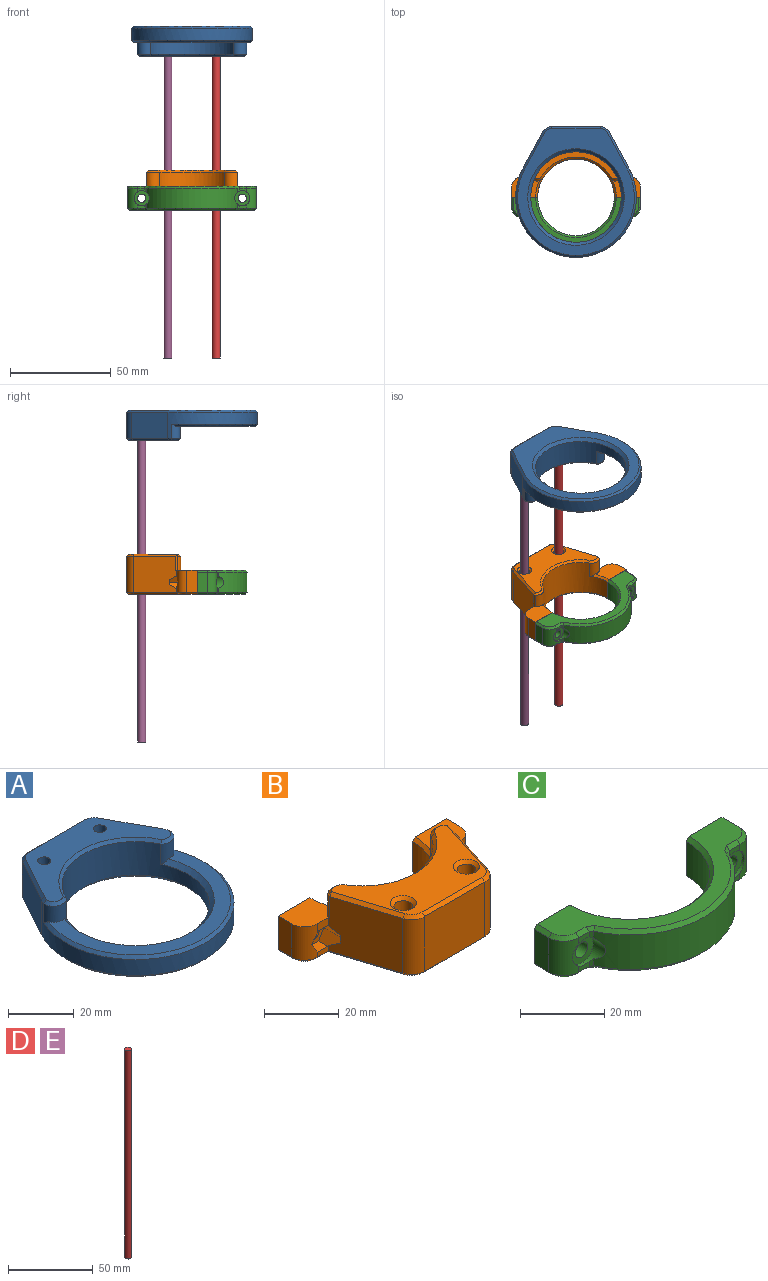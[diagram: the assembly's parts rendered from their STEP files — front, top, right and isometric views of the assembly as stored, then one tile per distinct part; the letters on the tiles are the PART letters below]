
ASSEMBLY  parts=5 mates=4
PART A: 39 faces, bbox 60x65x15 mm
  f0: plane 58x39.83mm, normal (0,0,1), area 508.6mm2, adj f11,f12,f17,f24
  f1: plane 17.96x13mm, normal (-0.88,0.48,0), area 266.4mm2, adj f2,f7,f20,f34
  f2: cylinder r=30mm len=60mm, axis (0,0,-1), area 771.3mm2, adj f1,f3,f18,f21,f24,f27,f32,f33
  f3: plane 17.96x13mm, normal (0.88,0.48,0), area 266.4mm2, adj f2,f4,f31,f35
  f4: cylinder r=5mm len=13mm, axis (0,0,-1), area 69.4mm2, adj f3,f5,f29,f37
  f5: plane 24.08x13mm, normal (0,1,0), area 313.1mm2, adj f4,f7,f26,f38
  f6: cylinder r=2mm len=13mm, axis (0,0,-1), area 163.4mm2, adj f13,f15
  f7: cylinder r=5mm len=13mm, axis (0,0,-1), area 69.4mm2, adj f1,f5,f23,f36
  f8: cylinder r=22.5mm len=45mm, axis (0,0,-1), area 1089.7mm2, adj f11,f12,f16,f17,f25
  f9: cylinder r=2mm len=13mm, axis (0,0,-1), area 163.4mm2, adj f13,f14
  f10: plane 63x58mm, normal (0,0,-1), area 1085mm2, adj f16,f33,f34,f35,f36,f37,f38
  f11: cylinder r=4mm len=7.5mm, axis (0,0,-1), area 59.8mm2, adj f0,f8,f17,f21,f22,f24
  f12: cylinder r=4mm len=7.5mm, axis (0,0,-1), area 59.8mm2, adj f0,f8,f17,f24,f27,f28
  f13: plane 52.4x24.64mm, normal (0,0,1), area 567.1mm2, adj f6,f9,f18,f20,f22,f23,f25,f26
  f14: plane 4x4mm, normal (0,0,1), area 12.6mm2, adj f9
  f15: plane 4x4mm, normal (0,0,1), area 12.6mm2, adj f6
  f16: cone r=24mm half-angle=45deg, axis (0,0,-1), area 309.9mm2, adj f8,f10
  f17: cone r=22.5mm half-angle=45deg, axis (0,0,1), area 193.2mm2, adj f0,f8,f11,f12
  f18: cone r=29mm half-angle=45deg, axis (0,0,-1), area 2.5mm2, adj f2,f13,f19,f20
  f19: plane 1x1mm, normal (-0.7,0.17,0.7), area 0.3mm2, adj f18,f21,f22
  f20: plane 18.44x10.75mm, normal (-0.62,0.34,0.71), area 29mm2, adj f1,f13,f18,f23
  f21: plane 7x0.41mm, normal (-0.97,0.23,0), area 2.9mm2, adj f2,f11,f19,f24
  f22: cone r=3mm half-angle=45deg, axis (0,0,-1), area 11.6mm2, adj f11,f13,f19,f25
  f23: cone r=4mm half-angle=45deg, axis (0,0,-1), area 6.8mm2, adj f7,f13,f20,f26
  f24: cone r=29mm half-angle=45deg, axis (0,0,-1), area 164.9mm2, adj f0,f2,f11,f12,f21,f27
  f25: cone r=22.5mm half-angle=45deg, axis (0,0,1), area 73.5mm2, adj f8,f13,f22,f28
  f26: plane 24.08x1mm, normal (0,0.71,0.71), area 34.1mm2, adj f5,f13,f23,f29
  f27: plane 7x0.41mm, normal (0.97,0.23,0), area 2.9mm2, adj f2,f12,f24,f30
  f28: cone r=4mm half-angle=45deg, axis (0,0,-1), area 11.6mm2, adj f12,f13,f25,f30
  f29: cone r=5mm half-angle=45deg, axis (0,0,-1), area 6.8mm2, adj f4,f13,f26,f31
  f30: plane 1x1mm, normal (0.7,0.17,0.7), area 0.3mm2, adj f27,f28,f32
  f31: plane 18.44x10.75mm, normal (0.62,0.34,0.71), area 29mm2, adj f3,f13,f29,f32
  f32: cone r=29mm half-angle=45deg, axis (0,0,-1), area 2.5mm2, adj f2,f13,f30,f31
  f33: cone r=30mm half-angle=45deg, axis (0,0,1), area 173mm2, adj f2,f10,f34,f35
  f34: plane 18.44x10.75mm, normal (-0.62,0.34,-0.71), area 29mm2, adj f1,f10,f33,f36
  f35: plane 18.44x10.75mm, normal (0.62,0.34,-0.71), area 29mm2, adj f3,f10,f33,f37
  f36: cone r=5mm half-angle=45deg, axis (0,0,1), area 6.8mm2, adj f7,f10,f34,f38
  f37: cone r=4mm half-angle=45deg, axis (0,0,1), area 6.8mm2, adj f4,f10,f35,f38
  f38: plane 24.08x1mm, normal (0,0.71,-0.71), area 34.1mm2, adj f5,f10,f36,f37
PART B: 70 faces, bbox 64x35x20 mm
  f0: plane 4.09x2.82mm, normal (0,-1,0), area 10.6mm2, adj f5,f11,f19,f52,f54,f56
  f1: plane 21.51x18mm, normal (0.95,-0.3,0), area 386.3mm2, adj f2,f3,f6,f14,f24,f26,f39,f60
  f2: plane 4.09x2.82mm, normal (0,-1,0), area 10.6mm2, adj f1,f4,f6,f61,f63,f64
  f3: plane 4.09x1.82mm, normal (0,-1,0), area 6.6mm2, adj f1,f4,f38,f62,f65,f66
  f4: cylinder r=5mm len=11mm, axis (0,0,-1), area 79.9mm2, adj f2,f3,f6,f15,f37,f63,f66
  f5: cylinder r=5mm len=11mm, axis (0,0,-1), area 79.9mm2, adj f0,f9,f10,f19,f43,f56,f57
  f6: plane 13.81x10.47mm, normal (0,0,1), area 115.7mm2, adj f1,f2,f4,f15,f17,f22,f24,f49
  f7: cylinder r=19mm len=38mm, axis (0,0,-1), area 907.6mm2, adj f8,f17,f21,f22,f29,f49,f50,f51
  f8: plane 13x12mm, normal (0,1,0), area 140.6mm2, adj f7,f9,f19,f20,f41,f50,f51,f69
  f9: plane 11x5mm, normal (-1,0,0), area 55mm2, adj f5,f8,f19,f41
  f10: plane 4.09x1.82mm, normal (0,-1,0), area 6.6mm2, adj f5,f11,f45,f53,f55,f57
  f11: plane 21.51x18mm, normal (-0.95,-0.3,0), area 386.3mm2, adj f0,f10,f12,f19,f31,f35,f46,f54
  f12: cylinder r=5mm len=18mm, axis (0,0,-1), area 113.8mm2, adj f11,f13,f33,f44
  f13: plane 22.68x18mm, normal (0,-1,0), area 408.2mm2, adj f12,f14,f30,f42
  f14: cylinder r=5mm len=18mm, axis (0,0,-1), area 113.8mm2, adj f1,f13,f28,f40
  f15: plane 11x5mm, normal (1,0,0), area 55mm2, adj f4,f6,f17,f36
  f16: cylinder r=2.5mm len=19mm, axis (0,0,-1), area 298.5mm2, adj f20,f48
  f17: plane 13x12mm, normal (0,1,0), area 140.6mm2, adj f6,f7,f15,f20,f36,f49,f51,f68
  f18: cylinder r=2.5mm len=19mm, axis (0,0,-1), area 298.5mm2, adj f20,f47
  f19: plane 13.81x10.47mm, normal (0,0,1), area 115.7mm2, adj f0,f5,f8,f9,f11,f21,f31,f50
  f20: plane 62x34mm, normal (0,0,-1), area 791.5mm2, adj f8,f16,f17,f18,f36,f37,f38,f39
  f21: cylinder r=3.94mm len=8mm, axis (0,0,-1), area 53.9mm2, adj f7,f19,f31,f32,f50
  f22: cylinder r=3.94mm len=8mm, axis (0,0,-1), area 53.9mm2, adj f6,f7,f24,f27,f49
  f23: plane 43.62x24.92mm, normal (0,0,1), area 546.7mm2, adj f26,f27,f28,f29,f30,f32,f33,f35
  f24: plane 7x0.93mm, normal (0.98,0.19,0), area 6.6mm2, adj f1,f6,f22,f25
  f25: plane 1x0.95mm, normal (0.74,0.14,0.66), area 0.6mm2, adj f24,f26,f27
  f26: plane 21.34x7.61mm, normal (0.67,-0.21,0.71), area 31.2mm2, adj f1,f23,f25,f28
  f27: cone r=2.94mm half-angle=45deg, axis (0,0,-1), area 9.2mm2, adj f22,f23,f25,f29
  f28: cone r=4mm half-angle=45deg, axis (0,0,-1), area 8mm2, adj f14,f23,f26,f30
  f29: cone r=19mm half-angle=45deg, axis (0,0,1), area 56.4mm2, adj f7,f23,f27,f32
  f30: plane 22.68x1mm, normal (0,-0.71,0.71), area 32.1mm2, adj f13,f23,f28,f33
  f31: plane 7x0.93mm, normal (-0.98,0.19,0), area 6.6mm2, adj f11,f19,f21,f34
  f32: cone r=3.94mm half-angle=45deg, axis (0,0,-1), area 9.2mm2, adj f21,f23,f29,f34
  f33: cone r=4mm half-angle=45deg, axis (0,0,-1), area 8mm2, adj f12,f23,f30,f35
  f34: plane 1x0.95mm, normal (-0.74,0.14,0.66), area 0.6mm2, adj f31,f32,f35
  f35: plane 21.34x7.61mm, normal (-0.67,-0.21,0.71), area 31.2mm2, adj f11,f23,f33,f34
  f36: plane 5x1mm, normal (0.71,0,-0.71), area 7.1mm2, adj f15,f17,f20,f37
  f37: cone r=4mm half-angle=45deg, axis (0,0,1), area 10mm2, adj f4,f20,f36,f38
  f38: plane 4.82x1mm, normal (0,-0.71,-0.71), area 6.3mm2, adj f3,f20,f37,f39
  f39: plane 22.51x7.76mm, normal (0.67,-0.21,-0.71), area 32.4mm2, adj f1,f20,f38,f40
  f40: cone r=5mm half-angle=45deg, axis (0,0,1), area 8mm2, adj f14,f20,f39,f42
  f41: plane 5x1mm, normal (-0.71,0,-0.71), area 7.1mm2, adj f8,f9,f20,f43
  f42: plane 22.68x1mm, normal (0,-0.71,-0.71), area 32.1mm2, adj f13,f20,f40,f44
  f43: cone r=4mm half-angle=45deg, axis (0,0,1), area 10mm2, adj f5,f20,f41,f45
  f44: cone r=5mm half-angle=45deg, axis (0,0,1), area 8mm2, adj f12,f20,f42,f46
  f45: plane 4.82x1mm, normal (0,-0.71,-0.71), area 6.3mm2, adj f10,f20,f43,f46
  f46: plane 22.51x7.76mm, normal (-0.67,-0.21,-0.71), area 32.4mm2, adj f11,f20,f44,f45
  f47: cone r=3.5mm half-angle=45deg, axis (0,0,1), area 26.7mm2, adj f18,f23
  f48: cone r=2.5mm half-angle=45deg, axis (0,0,1), area 26.7mm2, adj f16,f23
  f49: cone r=19mm half-angle=45deg, axis (0,0,1), area 12.9mm2, adj f6,f7,f17,f22
  f50: cone r=19mm half-angle=45deg, axis (0,0,1), area 12.9mm2, adj f7,f8,f19,f21
  f51: cone r=20mm half-angle=45deg, axis (0,0,-1), area 86.6mm2, adj f7,f8,f17,f20
  f52: plane 3.93x3.5mm, normal (0,0,-1), area 13.7mm2, adj f0,f54,f56,f58
  f53: plane 3.93x3.5mm, normal (0,0,1), area 13.7mm2, adj f10,f55,f57,f58
  f54: plane 7x3.4mm, normal (-0.87,0,-0.5), area 22.7mm2, adj f0,f11,f52,f55,f58,f59
  f55: plane 7x3.4mm, normal (-0.87,0,0.5), area 22.7mm2, adj f10,f11,f53,f54,f58,f59
  f56: plane 3.5x3.4mm, normal (0.87,0,-0.5), area 13.3mm2, adj f0,f5,f52,f57,f58
  f57: plane 3.5x3.4mm, normal (0.87,0,0.5), area 13.3mm2, adj f5,f10,f53,f56,f58
  f58: plane 7.85x6.8mm, normal (0,-1,0), area 26.2mm2, adj f52,f53,f54,f55,f56,f57,f69
  f59: plane 2.53x0.73mm, normal (0,1,0), area 0.9mm2, adj f11,f54,f55
  f60: plane 2.53x0.73mm, normal (0,1,0), area 0.9mm2, adj f1,f61,f62
  f61: plane 7x3.4mm, normal (0.87,0,-0.5), area 22.7mm2, adj f1,f2,f60,f62,f64,f67
  f62: plane 7x3.4mm, normal (0.87,0,0.5), area 22.7mm2, adj f1,f3,f60,f61,f65,f67
  f63: plane 3.5x3.4mm, normal (-0.87,0,-0.5), area 13.3mm2, adj f2,f4,f64,f66,f67
  f64: plane 3.93x3.5mm, normal (0,0,-1), area 13.7mm2, adj f2,f61,f63,f67
  f65: plane 3.93x3.5mm, normal (0,0,1), area 13.7mm2, adj f3,f62,f66,f67
  f66: plane 3.5x3.4mm, normal (-0.87,0,0.5), area 13.3mm2, adj f3,f4,f63,f65,f67
  f67: plane 7.85x6.8mm, normal (0,-1,0), area 26.2mm2, adj f61,f62,f63,f64,f65,f66,f68
  f68: cylinder r=2.1mm len=6.5mm, axis (0,-1,0), area 85.8mm2, adj f17,f67
  f69: cylinder r=2.1mm len=6.5mm, axis (0,-1,0), area 85.8mm2, adj f8,f58
PART C: 44 faces, bbox 64x25x12 mm
  f0: cylinder r=25mm len=45.3mm, axis (0,0,-1), area 541.1mm2, adj f1,f2,f3,f28,f32,f33,f40,f42
  f1: plane 2.04x0.93mm, normal (-0.54,-0.84,0), area 1.8mm2, adj f0,f4,f30,f40
  f2: plane 2.04x0.93mm, normal (-0.54,-0.84,0), area 1.8mm2, adj f0,f6,f25,f40
  f3: plane 2.04x0.93mm, normal (0.54,-0.84,0), area 1.8mm2, adj f0,f11,f34,f42
  f4: plane 3.44x1.77mm, normal (0,-1,0), area 4.6mm2, adj f1,f18,f27,f40
  f5: cylinder r=5mm len=10mm, axis (0,0,1), area 70.2mm2, adj f9,f11,f12,f26,f37,f42
  f6: plane 3.44x1.77mm, normal (0,-1,0), area 4.6mm2, adj f2,f18,f22,f40
  f7: cylinder r=2.1mm len=9mm, axis (0,-1,0), area 118.8mm2, adj f13,f43
  f8: cylinder r=2.1mm len=9mm, axis (0,-1,0), area 118.8mm2, adj f15,f41
  f9: plane 3.44x1.77mm, normal (0,-1,0), area 4.6mm2, adj f5,f29,f33,f42
  f10: plane 10x5mm, normal (-1,0,0), area 50mm2, adj f15,f18,f19,f21
  f11: plane 3.44x1.77mm, normal (0,-1,0), area 4.6mm2, adj f3,f5,f36,f42
  f12: plane 10x5mm, normal (1,0,0), area 50mm2, adj f5,f13,f23,f35
  f13: plane 13x12mm, normal (0,1,0), area 140.1mm2, adj f7,f12,f14,f16,f17,f23,f35,f38
  f14: cylinder r=19mm len=38mm, axis (0,0,-1), area 596.9mm2, adj f13,f15,f38,f39
  f15: plane 13x12mm, normal (0,1,0), area 140.1mm2, adj f8,f10,f14,f16,f17,f19,f21,f38
  f16: plane 62x24mm, normal (0,0,1), area 407.4mm2, adj f13,f15,f19,f20,f22,f23,f25,f26
  f17: plane 62x24mm, normal (0,0,-1), area 407.4mm2, adj f13,f15,f21,f24,f27,f30,f32,f34
  f18: cylinder r=5mm len=10mm, axis (0,0,1), area 70.2mm2, adj f4,f6,f10,f20,f24,f40
  f19: plane 5x1mm, normal (-0.71,0,0.71), area 7.1mm2, adj f10,f15,f16,f20
  f20: cone r=4mm half-angle=45deg, axis (0,0,-1), area 10mm2, adj f16,f18,f19,f22
  f21: plane 5x1mm, normal (-0.71,0,-0.71), area 7.1mm2, adj f10,f15,f17,f24
  f22: plane 3.44x1mm, normal (0,-0.71,0.71), area 4.9mm2, adj f6,f16,f20,f25
  f23: plane 5x1mm, normal (0.71,0,0.71), area 7.1mm2, adj f12,f13,f16,f26
  f24: cone r=4mm half-angle=45deg, axis (0,0,1), area 10mm2, adj f17,f18,f21,f27
  f25: plane 1.81x1.58mm, normal (-0.41,-0.64,0.64), area 2.1mm2, adj f2,f16,f22,f28
  f26: cone r=4mm half-angle=45deg, axis (0,0,-1), area 10mm2, adj f5,f16,f23,f29
  f27: plane 3.44x1mm, normal (0,-0.71,-0.71), area 4.9mm2, adj f4,f17,f24,f30
  f28: cone r=24mm half-angle=45deg, axis (0,0,-1), area 78.6mm2, adj f0,f16,f25,f31
  f29: plane 3.44x1mm, normal (0,-0.71,0.71), area 4.9mm2, adj f9,f16,f26,f31
  f30: plane 1.81x1.58mm, normal (-0.41,-0.64,-0.64), area 2.1mm2, adj f1,f17,f27,f32
  f31: plane 1.81x1.58mm, normal (0.41,-0.64,0.64), area 2.1mm2, adj f16,f28,f29,f33
  f32: cone r=25mm half-angle=45deg, axis (0,0,1), area 78.6mm2, adj f0,f17,f30,f34
  f33: plane 2.04x0.93mm, normal (0.54,-0.84,0), area 1.8mm2, adj f0,f9,f31,f42
  f34: plane 1.81x1.58mm, normal (0.41,-0.64,-0.64), area 2.1mm2, adj f3,f17,f32,f36
  f35: plane 5x1mm, normal (0.71,0,-0.71), area 7.1mm2, adj f12,f13,f17,f37
  f36: plane 3.44x1mm, normal (0,-0.71,-0.71), area 4.9mm2, adj f11,f17,f34,f37
  f37: cone r=4mm half-angle=45deg, axis (0,0,1), area 10mm2, adj f5,f17,f35,f36
  f38: cone r=20mm half-angle=45deg, axis (0,0,-1), area 86.6mm2, adj f13,f14,f15,f17
  f39: cone r=19mm half-angle=45deg, axis (0,0,1), area 86.6mm2, adj f13,f14,f15,f16
  f40: cylinder r=3.8mm len=7.6mm, axis (0,-1,0), area 39.6mm2, adj f0,f1,f2,f4,f6,f18,f41
  f41: plane 7.6x7.6mm, normal (0,-1,0), area 31.5mm2, adj f8,f40
  f42: cylinder r=3.8mm len=7.6mm, axis (0,-1,0), area 39.6mm2, adj f0,f3,f5,f9,f11,f33,f43
  f43: plane 7.6x7.6mm, normal (0,-1,0), area 31.5mm2, adj f7,f42
PART D: 3 faces, bbox 4x4x150 mm
  f0: cylinder r=2mm len=150mm, axis (0,0,-1), area 1885mm2, adj f1,f2
  f1: plane 4x4mm, normal (0,0,1), area 12.6mm2, adj f0
  f2: plane 4x4mm, normal (0,0,-1), area 12.6mm2, adj f0
PART E: same geometry as D
PLACE A rot(axis=(0,1,0),180deg) t=(-40.03,43.64,7.89)mm fixed
PLACE B rot(axis=(0,0,-1),180deg) t=(-40.03,43.64,-77.7)mm
PLACE C t=(-40.03,43.64,-77.7)mm
PLACE D t=(-28.03,71.13,-157.11)mm
PLACE E t=(-52.03,71.13,-157.11)mm
MATE slider E.f0 <-> B.f16  axis (0,0,-1) through (-52.03,71.13,-157.11)mm
MATE fastened D.f0 <-> A.f9  axis (0,0,1) through (-28.03,71.13,-7.11)mm
MATE fastened B.f68 <-> C.f8  axis (0,-1,0) through (-65.03,43.64,-77.7)mm
MATE fastened E.f0 <-> A.f6  axis (0,0,1) through (-52.03,71.13,-7.11)mm
